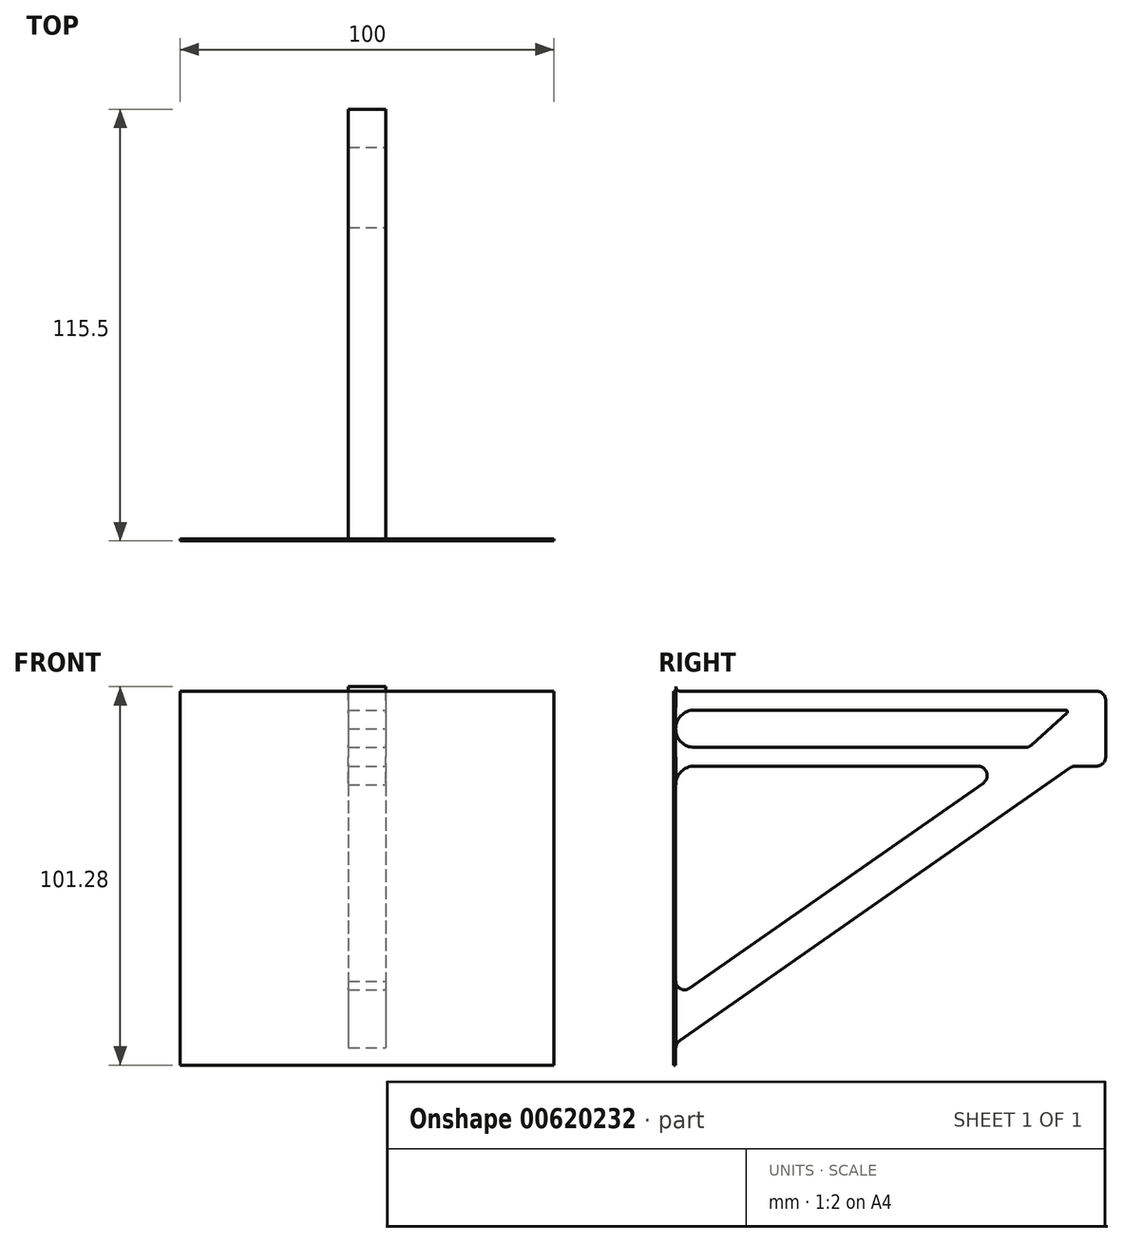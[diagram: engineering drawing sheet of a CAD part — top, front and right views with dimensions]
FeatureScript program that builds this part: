
annotation { "Feature Type Name" : "Feature", "Feature Type Description" : "" }
export const myFeature = defineFeature(function(context is Context, id is Id, definition is map)
    precondition{}
    {
        {
            var Q0;
            Q0=qCreatedBy(makeId("Front.planeOp"),FACE);
            var sketch = newSketch(context, id + "F0", { "sketchPlane" : qUnion([Q0])});
            skLineSegment(sketch, "E0.bottom", {"start": v(-50, -50) * mm, "end": v(50, -50) * mm});
            skLineSegment(sketch, "E0.top", {"start": v(-50, 50) * mm, "end": v(50, 50) * mm});
            skLineSegment(sketch, "E0.left", {"start": v(-50, -50) * mm, "end": v(-50, 50) * mm});
            skLineSegment(sketch, "E0.right", {"start": v(50, -50) * mm, "end": v(50, 50) * mm});
            skPoint(sketch, "E0.middle", {"position": v(0, 0) * mm});
            skSolve(sketch);
        }
        {
            var Q0;
            Q0=qCreatedBy(makeId("Right.planeOp"),FACE);
            var sketch = newSketch(context, id + "F1", { "sketchPlane" : qUnion([Q0])});
            skLineSegment(sketch, "E1", {"start": v(0, 40) * mm, "end": v(100, 40) * mm, "construction": true});
            skLineSegment(sketch, "E2", {"start": v(104.59, 44.13) * mm, "end": v(95.16, 35.64) * mm});
            skLineSegment(sketch, "E3", {"start": v(1.25, 50.06) * mm, "end": v(112.5, 50.06) * mm});
            skLineSegment(sketch, "E4.0", {"start": v(5, 45) * mm, "end": v(104.25, 45) * mm});
            skLineSegment(sketch, "E5.0", {"start": v(5, 35) * mm, "end": v(93.48, 35) * mm});
            skLineSegment(sketch, "E6.0", {"start": v(5.02, 30) * mm, "end": v(80.8, 30) * mm});
            skPoint(sketch, "E7.newPointB", {"position": v(0, 50.06) * mm});
            skArc(sketch, "E7.filletArc", {"start": v(0.02, 51.28) * mm, "mid": v(0.38, 50.42) * mm, "end": v(1.25, 50.06) * mm});
            skLineSegment(sketch, "E8", {"start": v(0, 40) * mm, "end": v(0, 40) * mm});
            skPoint(sketch, "E9.visualSharp", {"position": v(0, 45) * mm});
            skArc(sketch, "E9.filletArc", {"start": v(5, 45) * mm, "mid": v(1.47, 43.54) * mm, "end": v(0, 40.02) * mm});
            skPoint(sketch, "E10.visualSharp", {"position": v(0, 35) * mm});
            skArc(sketch, "E10.filletArc", {"start": v(0, 39.98) * mm, "mid": v(1.47, 36.46) * mm, "end": v(5, 35) * mm});
            skPoint(sketch, "E11.visualSharp", {"position": v(0, 30) * mm});
            skArc(sketch, "E11.filletArc", {"start": v(5.02, 30) * mm, "mid": v(1.49, 28.54) * mm, "end": v(0.02, 25) * mm});
            skLineSegment(sketch, "E12", {"start": v(115, 47.56) * mm, "end": v(115, 32.5) * mm});
            skLineSegment(sketch, "E13.0", {"start": v(105.54, 29.55) * mm, "end": v(1.09, -43.47) * mm});
            skLineSegment(sketch, "E14.0", {"start": v(82.22, 25.45) * mm, "end": v(3.7, -29.44) * mm});
            skArc(sketch, "E15.filletArc", {"start": v(0.05, -27.55) * mm, "mid": v(1.3, -29.6) * mm, "end": v(3.7, -29.44) * mm});
            skArc(sketch, "E16.filletArc", {"start": v(1.09, -43.47) * mm, "mid": v(0.36, -44.3) * mm, "end": v(0.1, -45.38) * mm});
            skLineSegment(sketch, "E17", {"start": v(0, 39.98) * mm, "end": v(0.02, 25) * mm});
            skLineSegment(sketch, "E18", {"start": v(0.05, -27.55) * mm, "end": v(0.1, -45.38) * mm});
            skLineSegment(sketch, "E19.trimOffspring", {"start": v(106.97, 30) * mm, "end": v(112.5, 30) * mm});
            skPoint(sketch, "E20.visualSharp", {"position": v(106.18, 30) * mm});
            skArc(sketch, "E20.filletArc", {"start": v(106.97, 30) * mm, "mid": v(106.22, 29.88) * mm, "end": v(105.54, 29.55) * mm});
            skPoint(sketch, "E21.visualSharp", {"position": v(88.73, 30) * mm});
            skArc(sketch, "E21.filletArc", {"start": v(82.22, 25.45) * mm, "mid": v(83.18, 28.25) * mm, "end": v(80.8, 30) * mm});
            skPoint(sketch, "E22.visualSharp", {"position": v(115, 30) * mm});
            skArc(sketch, "E22.filletArc", {"start": v(112.5, 30) * mm, "mid": v(114.27, 30.73) * mm, "end": v(115, 32.5) * mm});
            skPoint(sketch, "E23.visualSharp", {"position": v(115, 50.06) * mm});
            skArc(sketch, "E23.filletArc", {"start": v(115, 47.56) * mm, "mid": v(114.27, 49.33) * mm, "end": v(112.5, 50.06) * mm});
            skPoint(sketch, "E24.visualSharp", {"position": v(94.44, 35) * mm});
            skArc(sketch, "E24.filletArc", {"start": v(93.48, 35) * mm, "mid": v(94.38, 35.17) * mm, "end": v(95.16, 35.64) * mm});
            skPoint(sketch, "E25.visualSharp", {"position": v(105.56, 45) * mm});
            skArc(sketch, "E25.filletArc", {"start": v(104.59, 44.13) * mm, "mid": v(104.72, 44.68) * mm, "end": v(104.25, 45) * mm});
            skLineSegment(sketch, "E26", {"start": v(0.02, 51.28) * mm, "end": v(0, 40.02) * mm});
            skSolve(sketch);
        }
        {
            var Q0;
            Q0=sQuery(id+"F0.wireOp",VERTEX,"E0.left.start");
            var Q1;
            Q1=sQuery(id+"F0.wireOp",VERTEX,"E0.right.start");
            var Q2;
            Q2=sQuery(id+"F1.wireOp",VERTEX,"E2.start");
            var Q3;
            Q3 = qBodyType(qCreatedBy(id + "F3" ,EDGE), BodyType.WIRE);
            cPlane(context, id + "F2", {"entities" : qUnion([Q0, Q1, Q2, Q3]), "cplaneType" : CPlaneType.THREE_POINT, "offset" : 25 * mm, "width" : 150 * mm, "height" : 150 * mm});
        }
        {
            var Q0;
            Q0=qCreatedBy(id+"F2.planeOp",FACE);
            var sketch = newSketch(context, id + "F3", { "sketchPlane" : qUnion([Q0])});
            skCircle(sketch, "E27", {"center": v(0, -101.3) * mm, "radius": 5 * mm});
            skSolve(sketch);
        }
        {
            var Q0;
            Q0=makeQuery(id+"F1.imprint","IMPRINT",FACE,{"disambiguationData":[TD([[makeQuery(id+"F1.imprint","IMPRINT",EDGE,{"derivedFrom":sQuery(id+"F1.wireOp",EDGE,"E2")}),1.0]])]});
            var Q1;
            Q1 = qConstructionFilter(qBodyType(qCreatedBy(id + "F1" ,EDGE), BodyType.WIRE), ConstructionObject.NO);
            extrude(context, id + "F4", {"entities" : qUnion([Q0]), "surfaceEntities" : qUnion([Q1]), "endBound" : BoundingType.SYMMETRIC, "oppositeDirection" : true, "depth" : 10 * mm, "offsetDistance" : 25 * mm});
        }
        {
            var Q0;
            Q0=makeQuery(id+"F3.imprint","IMPRINT",FACE,{"disambiguationData":[TD([[makeQuery(id+"F3.imprint","IMPRINT",EDGE,{"derivedFrom":sQuery(id+"F3.wireOp",EDGE,"E27")}),1.0]])]});
            var Q1;
            Q1=sQuery(id+"F3.wireOp",EDGE,"E27");
            extrude(context, id + "F5", {"entities" : qUnion([Q0]), "bodyType" : ToolBodyType.SURFACE, "surfaceEntities" : qUnion([Q1]), "oppositeDirection" : true, "depth" : 0.5 * mm, "offsetDistance" : 25 * mm});
        }
        {
            var Q0;
            Q0 = qSketchRegion(id + "F0", true);
            extrude(context, id + "F6", {"entities" : qUnion([Q0]), "depth" : 0.5 * mm, "offsetDistance" : 25 * mm});
        }
    });
